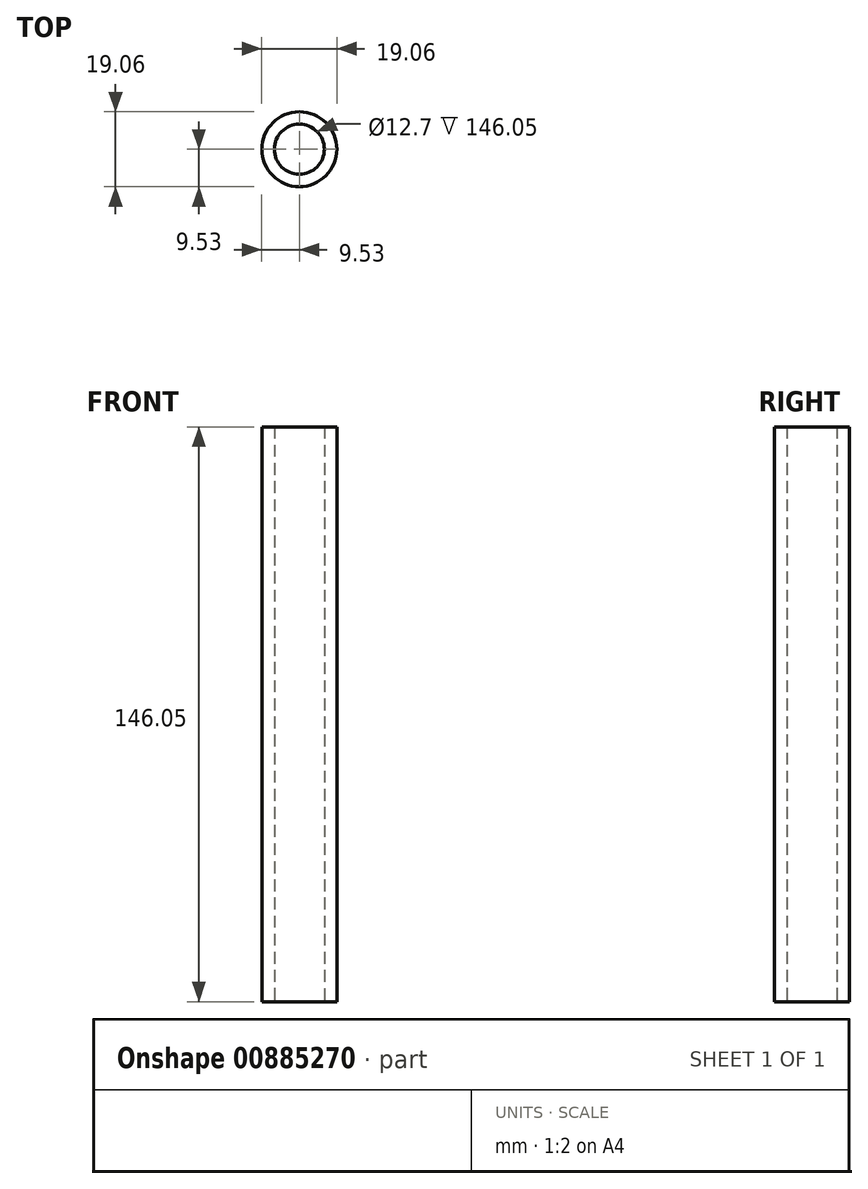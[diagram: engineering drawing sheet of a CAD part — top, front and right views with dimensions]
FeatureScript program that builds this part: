
annotation { "Feature Type Name" : "Feature", "Feature Type Description" : "" }
export const myFeature = defineFeature(function(context is Context, id is Id, definition is map)
    precondition{}
    {
        {
            var Q0;
            Q0=qCreatedBy(makeId("Top.planeOp"),FACE);
            var sketch = newSketch(context, id + "F0", { "sketchPlane" : qUnion([Q0])});
            skCircle(sketch, "E0", {"center": v(0, 0) * mm, "radius": 9.53 * mm});
            skCircle(sketch, "E1", {"center": v(0, 0) * mm, "radius": 6.35 * mm});
            skSolve(sketch);
        }
        {
            var Q0;
            Q0=makeQuery(id+"F0.imprint","IMPRINT",FACE,{"disambiguationData":[TD([[makeQuery(id+"F0.imprint","IMPRINT",EDGE,{"derivedFrom":sQuery(id+"F0.wireOp",EDGE,"E0")}),1.0]])]});
            extrude(context, id + "F1", {"entities" : qUnion([Q0]), "depth" : 146.05 * mm, "offsetDistance" : 25.4 * mm});
        }
    });
